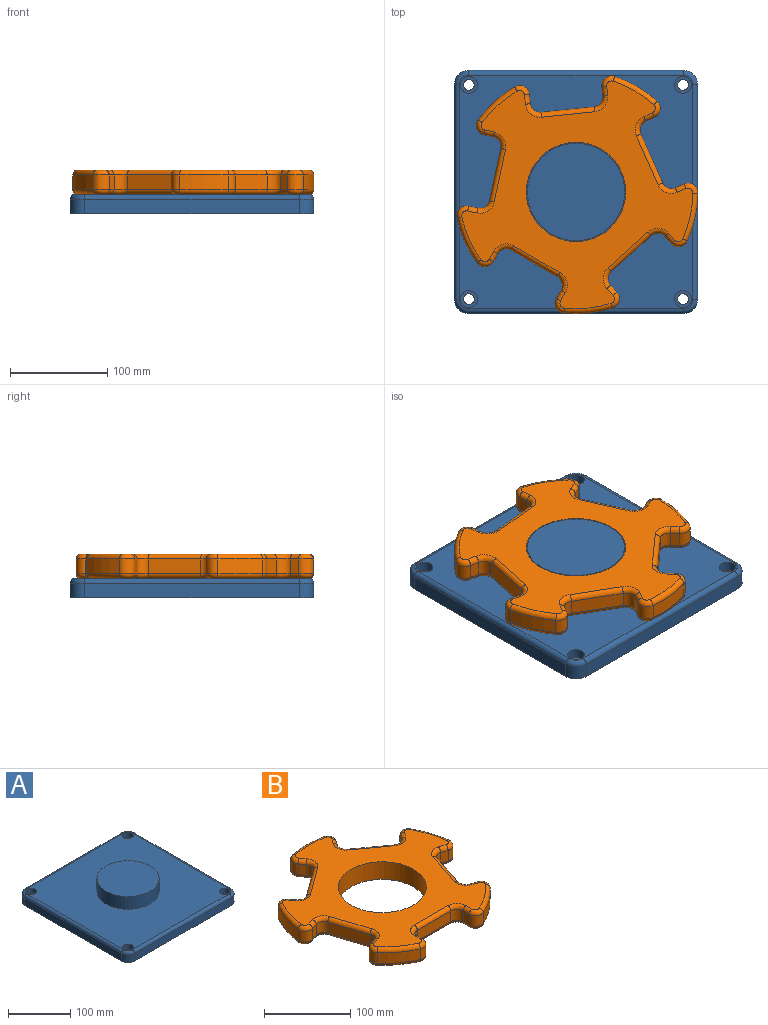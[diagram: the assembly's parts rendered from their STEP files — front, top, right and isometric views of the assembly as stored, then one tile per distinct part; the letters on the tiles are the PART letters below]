
ASSEMBLY  parts=2 mates=1
PART A: 32 faces, bbox 252.5x252.5x45 mm
  f0: plane 220x15mm, normal (1,0,0), area 3300mm2, adj f5,f8,f11,f27
  f1: plane 220x15mm, normal (0,1,0), area 3300mm2, adj f5,f8,f9,f31
  f2: plane 220x15mm, normal (-1,0,0), area 3300mm2, adj f5,f9,f10,f28
  f3: plane 220x15mm, normal (0,-1,0), area 3300mm2, adj f5,f10,f11,f24
  f4: plane 240x240mm, normal (0,0,1), area 48725.4mm2, adj f6,f14,f17,f20,f23,f24,f25,f26
  f5: plane 250x250mm, normal (0,0,-1), area 61926.7mm2, adj f0,f1,f2,f3,f8,f9,f10,f11
  f6: cylinder r=50mm len=100mm, axis (0,0,-1), area 7854mm2, adj f4,f7
  f7: plane 100x100mm, normal (0,0,1), area 7854mm2, adj f6
  f8: cylinder r=15mm len=15mm, axis (0,0,-1), area 353.4mm2, adj f0,f1,f5,f29
  f9: cylinder r=15mm len=15mm, axis (0,0,1), area 353.4mm2, adj f1,f2,f5,f30
  f10: cylinder r=15mm len=15mm, axis (0,0,-1), area 353.4mm2, adj f2,f3,f5,f26
  f11: cylinder r=15mm len=15mm, axis (0,0,1), area 353.4mm2, adj f0,f3,f5,f25
  f12: cylinder r=5.5mm len=11mm, axis (0,0,1), area 345.6mm2, adj f5,f13
  f13: plane 17.25x17.25mm, normal (0,0,1), area 138.7mm2, adj f12,f14
  f14: cylinder r=8.62mm len=17.25mm, axis (0,0,1), area 541.9mm2, adj f4,f13
  f15: cylinder r=5.5mm len=11mm, axis (0,0,1), area 345.6mm2, adj f5,f16
  f16: plane 17.25x17.25mm, normal (0,0,1), area 138.7mm2, adj f15,f17
  f17: cylinder r=8.62mm len=17.25mm, axis (0,0,1), area 541.9mm2, adj f4,f16
  f18: cylinder r=5.5mm len=11mm, axis (0,0,1), area 345.6mm2, adj f5,f19
  f19: plane 17.25x17.25mm, normal (0,0,1), area 138.7mm2, adj f18,f20
  f20: cylinder r=8.62mm len=17.25mm, axis (0,0,1), area 541.9mm2, adj f4,f19
  f21: cylinder r=5.5mm len=11mm, axis (0,0,1), area 345.6mm2, adj f5,f22
  f22: plane 17.25x17.25mm, normal (0,0,1), area 138.7mm2, adj f21,f23
  f23: cylinder r=8.62mm len=17.25mm, axis (0,0,1), area 541.9mm2, adj f4,f22
  f24: cylinder r=5mm len=220mm, axis (-1,0,0), area 1727.9mm2, adj f3,f4,f25,f26
  f25: torus R=10mm, axis (0,0,1), area 162.6mm2, adj f4,f11,f24,f27
  f26: torus R=10mm, axis (0,0,1), area 162.6mm2, adj f4,f10,f24,f28
  f27: cylinder r=5mm len=220mm, axis (0,-1,0), area 1727.9mm2, adj f0,f4,f25,f29
  f28: cylinder r=5mm len=220mm, axis (0,1,0), area 1727.9mm2, adj f2,f4,f26,f30
  f29: torus R=10mm, axis (0,0,1), area 162.6mm2, adj f4,f8,f27,f31
  f30: torus R=10mm, axis (0,0,1), area 162.6mm2, adj f4,f9,f28,f31
  f31: cylinder r=5mm len=220mm, axis (1,0,0), area 1727.9mm2, adj f1,f4,f29,f30
PART B: 123 faces, bbox 268.9x258.5x25 mm
  f0: plane 238.57x229.73mm, normal (0,0,1), area 21505.7mm2, adj f6,f83,f84,f85,f86,f87,f88,f89
  f1: plane 238.57x229.73mm, normal (0,0,-1), area 21505.7mm2, adj f6,f43,f44,f45,f46,f47,f48,f49
  f2: cylinder r=125mm len=47.82mm, axis (0,0,-1), area 759.5mm2, adj f34,f42,f74,f114
  f3: cylinder r=125mm len=50.29mm, axis (0,0,-1), area 759.5mm2, adj f27,f35,f75,f115
  f4: cylinder r=125mm len=47.82mm, axis (0,0,-1), area 759.5mm2, adj f20,f28,f59,f99
  f5: cylinder r=125mm len=40.68mm, axis (0,0,-1), area 759.5mm2, adj f13,f21,f43,f83
  f6: cylinder r=51mm len=102mm, axis (0,0,-1), area 8011.1mm2, adj f0,f1
  f7: cylinder r=125mm len=40.68mm, axis (0,0,-1), area 759.5mm2, adj f14,f41,f58,f98
  f8: plane 15x9.73mm, normal (-1,0,0), area 146mm2, adj f11,f14,f54,f94
  f9: plane 55x15mm, normal (0,-1,0), area 825mm2, adj f11,f12,f50,f90
  f10: plane 15x9.73mm, normal (1,0,0), area 146mm2, adj f12,f13,f46,f86
  f11: cylinder r=10mm len=15mm, axis (0,0,-1), area 235.6mm2, adj f8,f9,f52,f92
  f12: cylinder r=10mm len=15mm, axis (0,0,-1), area 235.6mm2, adj f9,f10,f48,f88
  f13: cylinder r=10mm len=15mm, axis (0,0,-1), area 299.5mm2, adj f5,f10,f44,f84
  f14: cylinder r=10mm len=15mm, axis (0,0,-1), area 299.5mm2, adj f7,f8,f56,f96
  f15: plane 15x9.26mm, normal (-0.31,0.95,0), area 146mm2, adj f18,f21,f47,f87
  f16: plane 52.31x17mm, normal (-0.95,-0.31,0), area 825mm2, adj f18,f19,f51,f91
  f17: plane 15x9.26mm, normal (0.31,-0.95,0), area 146mm2, adj f19,f20,f55,f95
  f18: cylinder r=10mm len=15mm, axis (0,0,-1), area 235.6mm2, adj f15,f16,f49,f89
  f19: cylinder r=10mm len=15mm, axis (0,0,-1), area 235.6mm2, adj f16,f17,f53,f93
  f20: cylinder r=10mm len=15mm, axis (0,0,-1), area 299.5mm2, adj f4,f17,f57,f97
  f21: cylinder r=10mm len=16.25mm, axis (0,0,-1), area 299.5mm2, adj f5,f15,f45,f85
  f22: plane 15x7.87mm, normal (0.81,0.59,0), area 146mm2, adj f25,f28,f63,f103
  f23: plane 44.5x32.33mm, normal (-0.59,0.81,0), area 825mm2, adj f25,f26,f67,f107
  f24: plane 15x7.87mm, normal (-0.81,-0.59,0), area 146mm2, adj f26,f27,f71,f111
  f25: cylinder r=10mm len=15mm, axis (0,0,-1), area 235.6mm2, adj f22,f23,f65,f105
  f26: cylinder r=10mm len=15mm, axis (0,0,-1), area 235.6mm2, adj f23,f24,f69,f109
  f27: cylinder r=10mm len=15.67mm, axis (0,0,-1), area 299.5mm2, adj f3,f24,f73,f113
  f28: cylinder r=10mm len=16.78mm, axis (0,0,-1), area 299.5mm2, adj f4,f22,f61,f101
  f29: plane 15x7.87mm, normal (0.81,-0.59,0), area 146mm2, adj f32,f35,f79,f119
  f30: plane 44.5x32.33mm, normal (0.59,0.81,0), area 825mm2, adj f32,f33,f82,f122
  f31: plane 15x7.87mm, normal (-0.81,0.59,0), area 146mm2, adj f33,f34,f78,f118
  f32: cylinder r=10mm len=15mm, axis (0,0,-1), area 235.6mm2, adj f29,f30,f81,f121
  f33: cylinder r=10mm len=15mm, axis (0,0,-1), area 235.6mm2, adj f30,f31,f80,f120
  f34: cylinder r=10mm len=16.78mm, axis (0,0,-1), area 299.5mm2, adj f2,f31,f76,f116
  f35: cylinder r=10mm len=15.67mm, axis (0,0,-1), area 299.5mm2, adj f3,f29,f77,f117
  f36: plane 15x9.26mm, normal (-0.31,-0.95,0), area 146mm2, adj f39,f42,f70,f110
  f37: plane 52.31x17mm, normal (0.95,-0.31,0), area 825mm2, adj f39,f40,f66,f106
  f38: plane 15x9.26mm, normal (0.31,0.95,0), area 146mm2, adj f40,f41,f62,f102
  f39: cylinder r=10mm len=15mm, axis (0,0,-1), area 235.6mm2, adj f36,f37,f68,f108
  f40: cylinder r=10mm len=15mm, axis (0,0,-1), area 235.6mm2, adj f37,f38,f64,f104
  f41: cylinder r=10mm len=16.25mm, axis (0,0,-1), area 299.5mm2, adj f7,f38,f60,f100
  f42: cylinder r=10mm len=15mm, axis (0,0,-1), area 299.5mm2, adj f2,f36,f72,f112
  f43: torus R=120mm, axis (0,0,1), area 391.9mm2, adj f1,f5,f44,f45
  f44: torus R=5mm, axis (0,0,1), area 128.3mm2, adj f1,f13,f43,f46
  f45: torus R=5mm, axis (0,0,1), area 128.3mm2, adj f1,f21,f43,f47
  f46: cylinder r=5mm len=9.73mm, axis (0,-1,0), area 76.4mm2, adj f1,f10,f44,f48
  f47: cylinder r=5mm len=10.8mm, axis (0.95,0.31,0), area 76.4mm2, adj f1,f15,f45,f49
  f48: torus R=15mm, axis (0,0,1), area 145.8mm2, adj f1,f12,f46,f50
  f49: torus R=15mm, axis (0,0,1), area 145.8mm2, adj f1,f18,f47,f51
  f50: cylinder r=5mm len=55mm, axis (-1,0,0), area 432mm2, adj f1,f9,f48,f52
  f51: cylinder r=5mm len=53.85mm, axis (-0.31,0.95,0), area 432mm2, adj f1,f16,f49,f53
  f52: torus R=15mm, axis (0,0,1), area 145.8mm2, adj f1,f11,f50,f54
  f53: torus R=15mm, axis (0,0,1), area 145.8mm2, adj f1,f19,f51,f55
  f54: cylinder r=5mm len=9.73mm, axis (0,1,0), area 76.4mm2, adj f1,f8,f52,f56
  f55: cylinder r=5mm len=10.8mm, axis (-0.95,-0.31,0), area 76.4mm2, adj f1,f17,f53,f57
  f56: torus R=5mm, axis (0,0,1), area 128.3mm2, adj f1,f14,f54,f58
  f57: torus R=5mm, axis (0,0,1), area 128.3mm2, adj f1,f20,f55,f59
  f58: torus R=120mm, axis (0,0,1), area 391.9mm2, adj f1,f7,f56,f60
  f59: torus R=120mm, axis (0,0,1), area 391.9mm2, adj f1,f4,f57,f61
  f60: torus R=5mm, axis (0,0,1), area 128.3mm2, adj f1,f41,f58,f62
  f61: torus R=5mm, axis (0,0,1), area 128.3mm2, adj f1,f28,f59,f63
  f62: cylinder r=5mm len=10.8mm, axis (0.95,-0.31,0), area 76.4mm2, adj f1,f38,f60,f64
  f63: cylinder r=5mm len=10.81mm, axis (0.59,-0.81,0), area 76.4mm2, adj f1,f22,f61,f65
  f64: torus R=15mm, axis (0,0,1), area 145.8mm2, adj f1,f40,f62,f66
  f65: torus R=15mm, axis (0,0,1), area 145.8mm2, adj f1,f25,f63,f67
  f66: cylinder r=5mm len=53.85mm, axis (-0.31,-0.95,0), area 432mm2, adj f1,f37,f64,f68
  f67: cylinder r=5mm len=47.44mm, axis (0.81,0.59,0), area 432mm2, adj f1,f23,f65,f69
  f68: torus R=15mm, axis (0,0,1), area 145.8mm2, adj f1,f39,f66,f70
  f69: torus R=15mm, axis (0,0,1), area 145.8mm2, adj f1,f26,f67,f71
  f70: cylinder r=5mm len=10.8mm, axis (-0.95,0.31,0), area 76.4mm2, adj f1,f36,f68,f72
  f71: cylinder r=5mm len=10.81mm, axis (-0.59,0.81,0), area 76.4mm2, adj f1,f24,f69,f73
  f72: torus R=5mm, axis (0,0,1), area 128.3mm2, adj f1,f42,f70,f74
  f73: torus R=5mm, axis (0,0,1), area 128.3mm2, adj f1,f27,f71,f75
  f74: torus R=120mm, axis (0,0,1), area 391.9mm2, adj f1,f2,f72,f76
  f75: torus R=120mm, axis (0,0,1), area 391.9mm2, adj f1,f3,f73,f77
  f76: torus R=5mm, axis (0,0,1), area 128.3mm2, adj f1,f34,f74,f78
  f77: torus R=5mm, axis (0,0,1), area 128.3mm2, adj f1,f35,f75,f79
  f78: cylinder r=5mm len=10.81mm, axis (0.59,0.81,0), area 76.4mm2, adj f1,f31,f76,f80
  f79: cylinder r=5mm len=10.81mm, axis (-0.59,-0.81,0), area 76.4mm2, adj f1,f29,f77,f81
  f80: torus R=15mm, axis (0,0,1), area 145.8mm2, adj f1,f33,f78,f82
  f81: torus R=15mm, axis (0,0,1), area 145.8mm2, adj f1,f32,f79,f82
  f82: cylinder r=5mm len=47.44mm, axis (0.81,-0.59,0), area 432mm2, adj f1,f30,f80,f81
  f83: torus R=120mm, axis (0,0,1), area 391.9mm2, adj f0,f5,f84,f85
  f84: torus R=5mm, axis (0,0,1), area 128.3mm2, adj f0,f13,f83,f86
  f85: torus R=5mm, axis (0,0,1), area 128.3mm2, adj f0,f21,f83,f87
  f86: cylinder r=5mm len=9.73mm, axis (0,1,0), area 76.4mm2, adj f0,f10,f84,f88
  f87: cylinder r=5mm len=10.8mm, axis (-0.95,-0.31,0), area 76.4mm2, adj f0,f15,f85,f89
  f88: torus R=15mm, axis (0,0,1), area 145.8mm2, adj f0,f12,f86,f90
  f89: torus R=15mm, axis (0,0,1), area 145.8mm2, adj f0,f18,f87,f91
  f90: cylinder r=5mm len=55mm, axis (1,0,0), area 432mm2, adj f0,f9,f88,f92
  f91: cylinder r=5mm len=53.85mm, axis (0.31,-0.95,0), area 432mm2, adj f0,f16,f89,f93
  f92: torus R=15mm, axis (0,0,1), area 145.8mm2, adj f0,f11,f90,f94
  f93: torus R=15mm, axis (0,0,1), area 145.8mm2, adj f0,f19,f91,f95
  f94: cylinder r=5mm len=9.73mm, axis (0,-1,0), area 76.4mm2, adj f0,f8,f92,f96
  f95: cylinder r=5mm len=10.8mm, axis (0.95,0.31,0), area 76.4mm2, adj f0,f17,f93,f97
  f96: torus R=5mm, axis (0,0,1), area 128.3mm2, adj f0,f14,f94,f98
  f97: torus R=5mm, axis (0,0,1), area 128.3mm2, adj f0,f20,f95,f99
  f98: torus R=120mm, axis (0,0,1), area 391.9mm2, adj f0,f7,f96,f100
  f99: torus R=120mm, axis (0,0,1), area 391.9mm2, adj f0,f4,f97,f101
  f100: torus R=5mm, axis (0,0,1), area 128.3mm2, adj f0,f41,f98,f102
  f101: torus R=5mm, axis (0,0,1), area 128.3mm2, adj f0,f28,f99,f103
  f102: cylinder r=5mm len=10.8mm, axis (-0.95,0.31,0), area 76.4mm2, adj f0,f38,f100,f104
  f103: cylinder r=5mm len=10.81mm, axis (-0.59,0.81,0), area 76.4mm2, adj f0,f22,f101,f105
  f104: torus R=15mm, axis (0,0,1), area 145.8mm2, adj f0,f40,f102,f106
  f105: torus R=15mm, axis (0,0,1), area 145.8mm2, adj f0,f25,f103,f107
  f106: cylinder r=5mm len=53.85mm, axis (0.31,0.95,0), area 432mm2, adj f0,f37,f104,f108
  f107: cylinder r=5mm len=47.44mm, axis (-0.81,-0.59,0), area 432mm2, adj f0,f23,f105,f109
  f108: torus R=15mm, axis (0,0,1), area 145.8mm2, adj f0,f39,f106,f110
  f109: torus R=15mm, axis (0,0,1), area 145.8mm2, adj f0,f26,f107,f111
  f110: cylinder r=5mm len=10.8mm, axis (0.95,-0.31,0), area 76.4mm2, adj f0,f36,f108,f112
  f111: cylinder r=5mm len=10.81mm, axis (0.59,-0.81,0), area 76.4mm2, adj f0,f24,f109,f113
  f112: torus R=5mm, axis (0,0,1), area 128.3mm2, adj f0,f42,f110,f114
  f113: torus R=5mm, axis (0,0,1), area 128.3mm2, adj f0,f27,f111,f115
  f114: torus R=120mm, axis (0,0,1), area 391.9mm2, adj f0,f2,f112,f116
  f115: torus R=120mm, axis (0,0,1), area 391.9mm2, adj f0,f3,f113,f117
  f116: torus R=5mm, axis (0,0,1), area 128.3mm2, adj f0,f34,f114,f118
  f117: torus R=5mm, axis (0,0,1), area 128.3mm2, adj f0,f35,f115,f119
  f118: cylinder r=5mm len=10.81mm, axis (-0.59,-0.81,0), area 76.4mm2, adj f0,f31,f116,f120
  f119: cylinder r=5mm len=10.81mm, axis (0.59,0.81,0), area 76.4mm2, adj f0,f29,f117,f121
  f120: torus R=15mm, axis (0,0,1), area 145.8mm2, adj f0,f33,f118,f122
  f121: torus R=15mm, axis (0,0,1), area 145.8mm2, adj f0,f32,f119,f122
  f122: cylinder r=5mm len=47.44mm, axis (-0.81,0.59,0), area 432mm2, adj f0,f30,f120,f121
PLACE A at identity fixed
PLACE B rot(axis=(0,0,-1),174.1deg) t=(0,0,0)mm
MATE revolute A.f6 <-> B.f2  axis (0,0,1) through (0,0,45)mm
